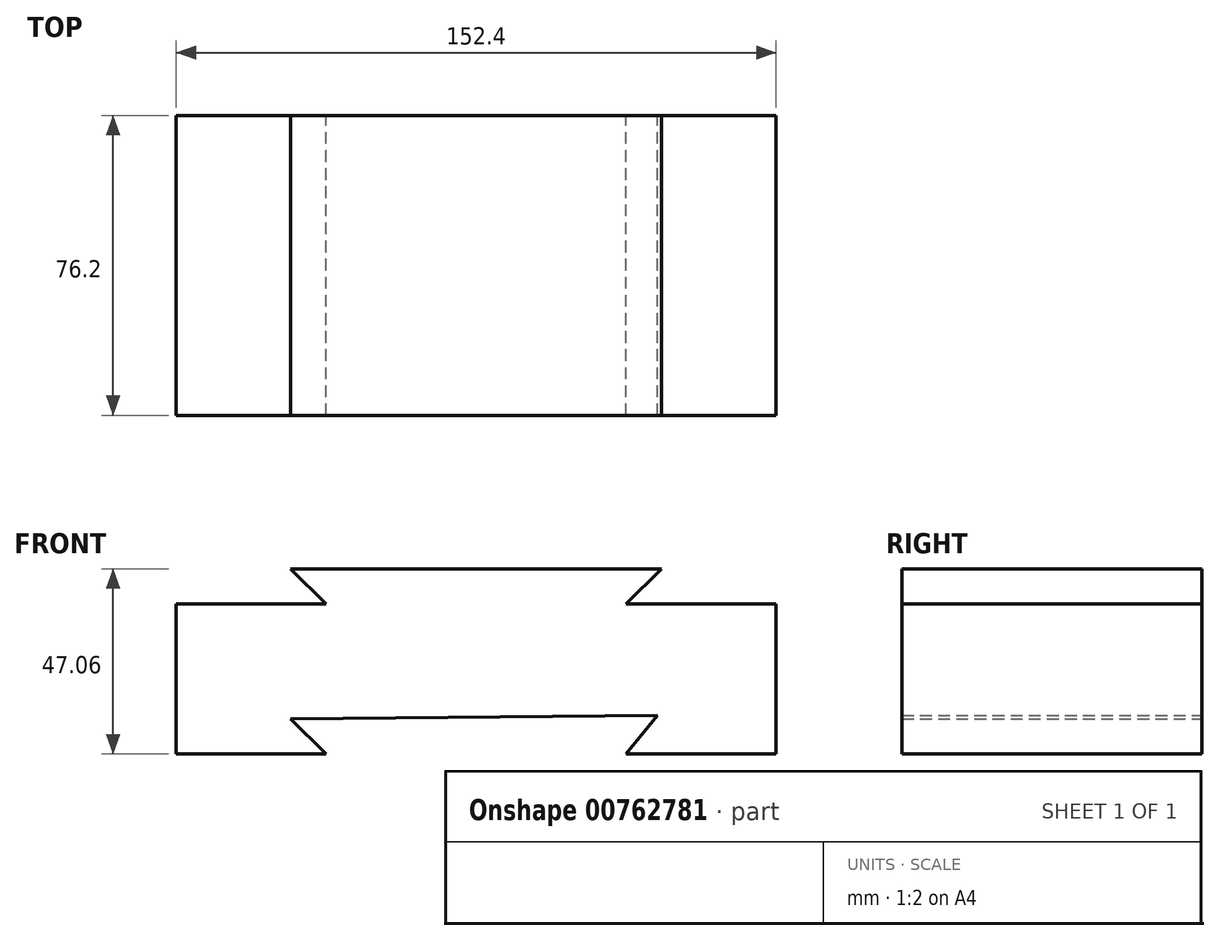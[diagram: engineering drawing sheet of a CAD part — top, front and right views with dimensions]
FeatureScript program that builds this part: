
annotation { "Feature Type Name" : "Feature", "Feature Type Description" : "" }
export const myFeature = defineFeature(function(context is Context, id is Id, definition is map)
    precondition{}
    {
        {
            var Q0;
            Q0=qCreatedBy(makeId("Front.planeOp"),FACE);
            var sketch = newSketch(context, id + "F0", { "sketchPlane" : qUnion([Q0])});
            skLineSegment(sketch, "E0", {"start": v(25.76, -22.4) * mm, "end": v(17.74, -32.24) * mm});
            skLineSegment(sketch, "E1", {"start": v(17.74, -32.24) * mm, "end": v(55.84, -32.24) * mm});
            skLineSegment(sketch, "E2", {"start": v(55.84, -32.24) * mm, "end": v(55.84, 5.86) * mm});
            skLineSegment(sketch, "E3", {"start": v(55.84, 5.86) * mm, "end": v(17.74, 5.86) * mm});
            skLineSegment(sketch, "E4", {"start": v(17.74, 5.86) * mm, "end": v(26.74, 14.82) * mm});
            skLineSegment(sketch, "E5", {"start": v(26.74, 14.82) * mm, "end": v(-67.46, 14.82) * mm});
            skLineSegment(sketch, "E6", {"start": v(-67.46, 14.82) * mm, "end": v(-58.46, 5.86) * mm});
            skLineSegment(sketch, "E7", {"start": v(-58.46, 5.86) * mm, "end": v(-96.56, 5.86) * mm});
            skLineSegment(sketch, "E8", {"start": v(-96.56, 5.86) * mm, "end": v(-96.56, -32.24) * mm});
            skLineSegment(sketch, "E9", {"start": v(-96.56, -32.24) * mm, "end": v(-58.46, -32.24) * mm});
            skLineSegment(sketch, "E10", {"start": v(-58.46, -32.24) * mm, "end": v(-67.46, -23.28) * mm});
            skLineSegment(sketch, "E11", {"start": v(-67.46, -23.28) * mm, "end": v(25.76, -22.4) * mm});
            skSolve(sketch);
        }
        {
            var Q0;
            Q0=makeQuery(id+"F0.imprint","IMPRINT",FACE,{"disambiguationData":[TD([[makeQuery(id+"F0.imprint","IMPRINT",EDGE,{"derivedFrom":sQuery(id+"F0.wireOp",EDGE,"E0")}),1.0]])]});
            extrude(context, id + "F1", {"entities" : qUnion([Q0]), "depth" : 76.2 * mm, "offsetDistance" : 25.4 * mm});
        }
    });
